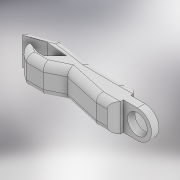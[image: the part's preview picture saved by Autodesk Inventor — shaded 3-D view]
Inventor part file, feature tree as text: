
AUTODESK INVENTOR PART (.ipt)
format: ipt  version: 2022 (Build 260153000, 153)  size: 242,176 bytes
history: native  units: mm
features: extrude x5, sketch x4, fillet x3, projected_geometry x3, plane x2, chamfer x1
ambient origin geometry x8: Origin, YZ Plane, XZ Plane, XY Plane, X Axis, Y Axis, Z Axis, Center Point
bodies: Body1 (feature_tree)
feature tree (18):
  extrude  "Extrusion1"  Depth=2.25mm
  plane  "Work Plane3"
  fillet  "Fillet5"  Radius=2.25mm
  sketch  "Sketch9"  dims[d38=4.25mm d39=8.5mm d40=0.0mm]
  extrude  "Extrusion6"  Depth=8.5mm TaperAngle=0.0deg
  extrude  "Extrusion7"  Depth=8.5mm TaperAngle=0.0deg
  plane  "Work Plane4"
  extrude  "Extrusion8"  Depth=8.5mm TaperAngle=0.0deg
  extrude  "Extrusion9"  Depth=2.0mm TaperAngle=45.0deg
  chamfer  "Chamfer3"  Distance=2.0mm
  fillet  "Fillet6"  Radius=2.0mm
  fillet  "Fillet7"  [1 undecoded]
  sketch  "Sketch4"  dims[d14=8.5mm d15=0.0mm d24=8.0mm d25=2.25mm]
  projected_geometry  "Projected Loop6"
  projected_geometry  "Projected Loop7"
  sketch  "Sketch10"  dims[d41=8.5mm d42=0.0mm d43=8.5mm d44=0.0mm]
  projected_geometry  "Projected Loop8"
  sketch  "Sketch11"  dims[d45=6.0mm d46=8.5mm d47=0.0mm d48=2.0mm d49=2.0mm d50=45.0deg d51=2.0mm d52=2.0mm]
note: 1 required parameter value undecoded (feature->parameter linkage not recoverable at this tier; creation-order binding heuristic only, values carry confidence <= 0.55)
